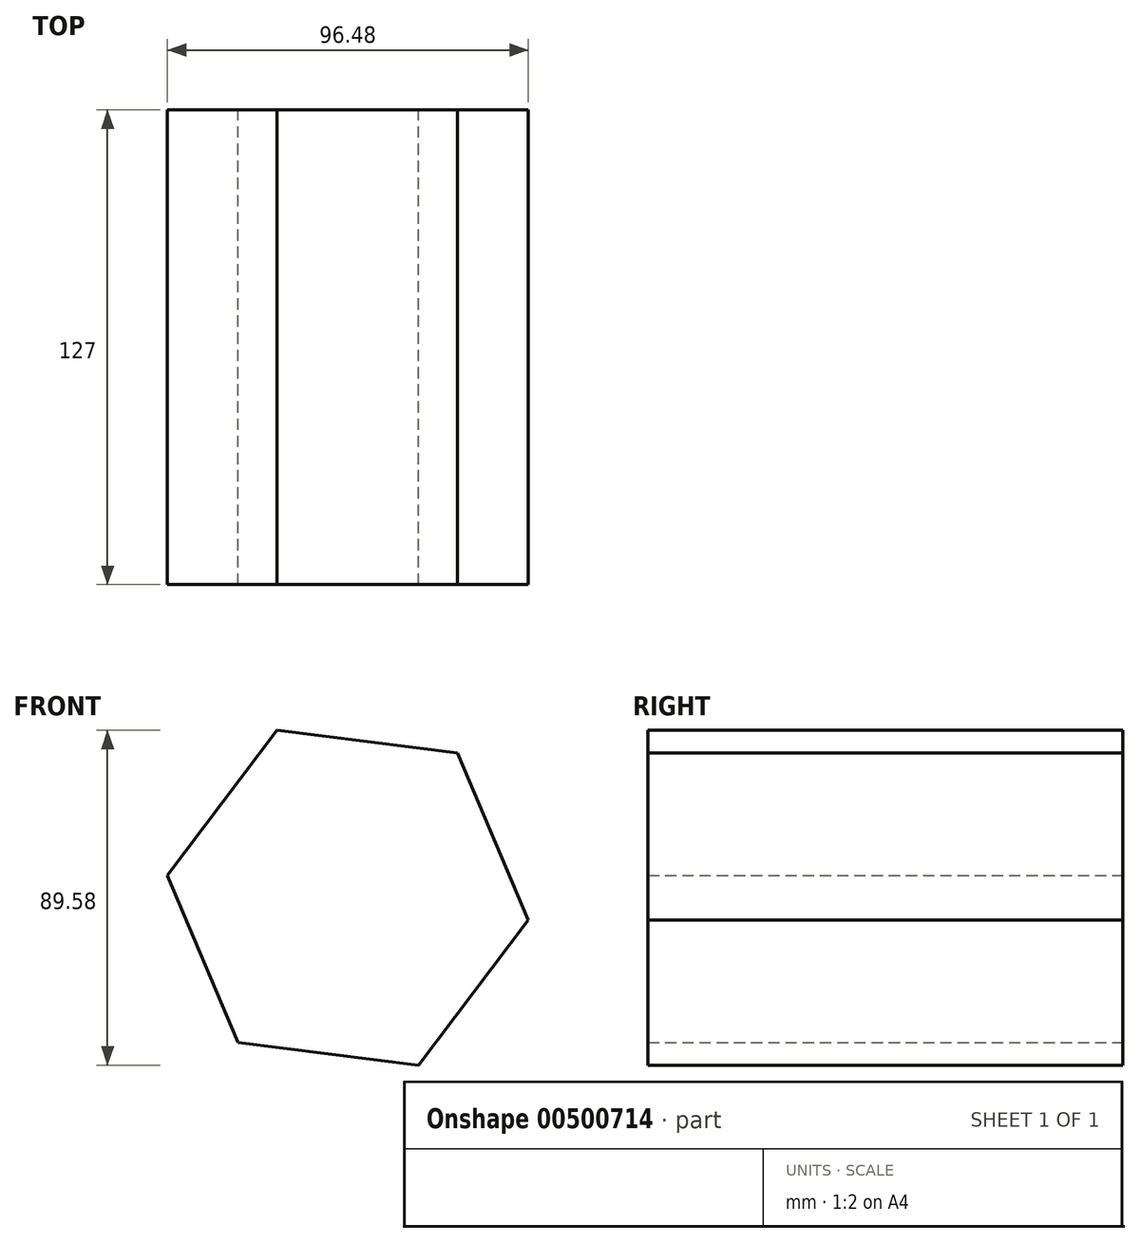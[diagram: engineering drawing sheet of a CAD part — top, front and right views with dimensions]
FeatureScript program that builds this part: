
annotation { "Feature Type Name" : "Feature", "Feature Type Description" : "" }
export const myFeature = defineFeature(function(context is Context, id is Id, definition is map)
    precondition{}
    {
        {
            var Q0;
            Q0=qCreatedBy(makeId("Front.planeOp"),FACE);
            var sketch = newSketch(context, id + "F0", { "sketchPlane" : qUnion([Q0])});
            skCircle(sketch, "E0.cCircle", {"center": v(0, 0) * mm, "radius": 48.62 * mm, "construction": true});
            skLineSegment(sketch, "E0.0", {"start": v(29.33, 38.77) * mm, "end": v(48.24, -6.02) * mm});
            skLineSegment(sketch, "E0.1", {"start": v(48.24, -6.02) * mm, "end": v(18.91, -44.79) * mm});
            skLineSegment(sketch, "E0.2", {"start": v(18.91, -44.79) * mm, "end": v(-29.33, -38.77) * mm});
            skLineSegment(sketch, "E0.3", {"start": v(-29.33, -38.77) * mm, "end": v(-48.24, 6.02) * mm});
            skLineSegment(sketch, "E0.4", {"start": v(-48.24, 6.02) * mm, "end": v(-18.91, 44.79) * mm});
            skLineSegment(sketch, "E0.5", {"start": v(-18.91, 44.79) * mm, "end": v(29.33, 38.77) * mm});
            skSolve(sketch);
        }
        {
            var Q0;
            Q0=makeQuery(id+"F0.imprint","IMPRINT",FACE,{"disambiguationData":[TD([[makeQuery(id+"F0.imprint","IMPRINT",EDGE,{"derivedFrom":sQuery(id+"F0.wireOp",EDGE,"E0.0")}),-1.0]])]});
            extrude(context, id + "F1", {"entities" : qUnion([Q0]), "depth" : 127 * mm});
        }
    });
